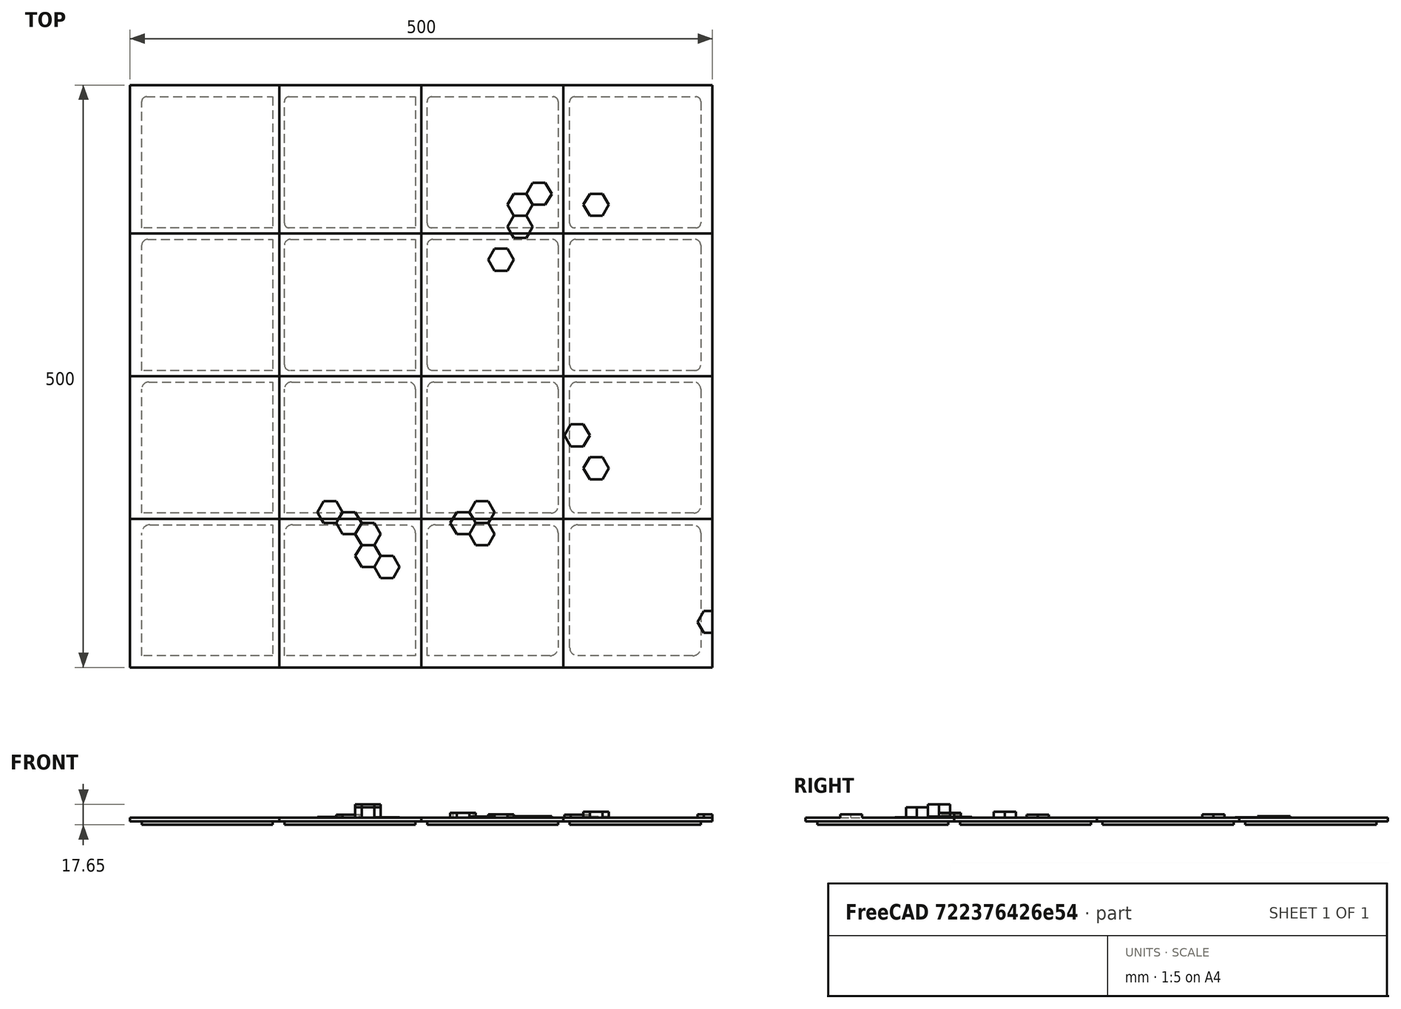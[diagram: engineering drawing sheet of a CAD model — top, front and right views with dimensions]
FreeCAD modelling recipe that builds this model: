
FCSTD DOCUMENT  (FreeCAD 0.17R13541 (Git))
Label: division_map_positive
License: All rights reserved
LicenseURL: http://en.wikipedia.org/wiki/All_rights_reserved
objects: Drawing::FeatureViewPart×48, Part::MultiCommon×16, Part::Mirroring×12, Part::Extrusion×4, Part::FeaturePython×2, Part::Cut×1, Drawing::FeaturePage×1
note: 35 computed .brp shape members not serialized (recipe doc carries the construction recipe); baked Part::Feature solids carry a one-line shape summary decoded from their .brp

FEATURE [Part::FeaturePython] Clone  label="Body001"  # WARN: FeaturePython — macro-defined, semantics opaque (R4)
  AttacherType = Attacher::AttachEngine3D
  Fuse = false
  Placement = pos=(0,0,3) rot=(0,0,1;0rad)
  Scale = (1,1,1)
FEATURE [Part::FeaturePython] Clone002  # WARN: FeaturePython — macro-defined, semantics opaque (R4)
  AttacherType = Attacher::AttachEngine3D
  Fuse = false
  Placement = pos=(0,0,0) rot=(0,0,1;1.5708rad)
  Scale = (1,1,1)
FEATURE [Part::Extrusion] Extrude  label="A1"
  Dir = (0,0,1)
  DirMode = 2
  FaceMakerClass = Part::FaceMakerBullseye
  LengthFwd = 50
  LengthRev = 0
  Solid = true
  Symmetric = true
FEATURE [Part::Extrusion] Extrude001  label="B1"
  Dir = (0,0,1)
  DirMode = 2
  FaceMakerClass = Part::FaceMakerBullseye
  LengthFwd = 50
  LengthRev = 0
  Solid = true
  Symmetric = true
FEATURE [Part::Extrusion] Extrude003  label="A2"
  Dir = (0,0,1)
  DirMode = 2
  FaceMakerClass = Part::FaceMakerBullseye
  LengthFwd = 50
  LengthRev = 0
  Solid = true
  Symmetric = true
FEATURE [Part::Extrusion] Extrude002  label="B2"
  Dir = (0,0,1)
  DirMode = 2
  FaceMakerClass = Part::FaceMakerBullseye
  LengthFwd = 70
  LengthRev = 0
  Solid = true
  Symmetric = true
FEATURE [Part::Mirroring] Part__Mirroring007  label="B3"
  Base = (0,0,0)
  Normal = (1,0,0)
  Source = -> Extrude002
FEATURE [Part::Mirroring] Part__Mirroring010  label="A3"
  Base = (0,0,0)
  Normal = (1,0,0)
  Source = -> Extrude003
FEATURE [Part::Mirroring] Part__Mirroring001  label="A4"
  Base = (0,0,0)
  Normal = (1,0,0)
  Source = -> Extrude
FEATURE [Part::Mirroring] Part__Mirroring004  label="B4"
  Base = (0,0,0)
  Normal = (1,0,0)
  Source = -> Extrude001
FEATURE [Part::Mirroring] Part__Mirroring006  label="C2"
  Base = (0,0,0)
  Normal = (0,1,0)
  Source = -> Extrude002
FEATURE [Part::Mirroring] Part__Mirroring008  label="C3"
  Base = (0,0,0)
  Normal = (1,0,0)
  Source = -> Part__Mirroring006
FEATURE [Part::Mirroring] Part__Mirroring003  label="C1"
  Base = (0,0,0)
  Normal = (0,1,0)
  Source = -> Extrude001
FEATURE [Part::Mirroring] Part__Mirroring005  label="C4"
  Base = (0,0,0)
  Normal = (1,0,0)
  Source = -> Part__Mirroring003
FEATURE [Part::Mirroring] Part__Mirroring  label="D1"
  Base = (0,0,0)
  Normal = (0,1,0)
  Source = -> Extrude
FEATURE [Part::Mirroring] Part__Mirroring009  label="D2"
  Base = (0,0,0)
  Normal = (0,1,0)
  Source = -> Extrude003
FEATURE [Part::Mirroring] Part__Mirroring011  label="D3"
  Base = (0,0,0)
  Normal = (1,0,0)
  Source = -> Part__Mirroring009
FEATURE [Part::Mirroring] Part__Mirroring002  label="D4"
  Base = (0,0,0)
  Normal = (1,0,0)
  Source = -> Part__Mirroring
FEATURE [Part::Cut] Cut  label="data_map"
  Base = -> Clone002
  Tool = -> Clone
FEATURE [Part::MultiCommon] Common  label="A1_cut"
  Shapes = -> [Extrude,Cut]
FEATURE [Part::MultiCommon] Common001  label="A2_cut"
  Shapes = -> [Cut,Extrude003]
FEATURE [Part::MultiCommon] Common002  label="A3_cut"
  Shapes = -> [Cut,Part__Mirroring010]
FEATURE [Part::MultiCommon] Common003  label="A4_cut"
  Shapes = -> [Cut,Part__Mirroring001]
FEATURE [Part::MultiCommon] Common004  label="B1_cut"
  Shapes = -> [Cut,Extrude001]
FEATURE [Part::MultiCommon] Common005  label="B2_cut"
  Shapes = -> [Extrude002,Cut]
FEATURE [Part::MultiCommon] Common006  label="B3_cut"
  Shapes = -> [Cut,Part__Mirroring007]
FEATURE [Part::MultiCommon] Common007  label="B4_cut"
  Shapes = -> [Cut,Part__Mirroring004]
FEATURE [Part::MultiCommon] Common008  label="C1_cut"
  Shapes = -> [Cut,Part__Mirroring003]
FEATURE [Part::MultiCommon] Common009  label="C2_cut"
  Shapes = -> [Cut,Part__Mirroring006]
FEATURE [Part::MultiCommon] Common010  label="C3_cut"
  Shapes = -> [Cut,Part__Mirroring008]
FEATURE [Part::MultiCommon] Common011  label="C4_cut"
  Shapes = -> [Cut,Part__Mirroring005]
FEATURE [Part::MultiCommon] Common012  label="D1_cut"
  Shapes = -> [Cut,Part__Mirroring]
FEATURE [Part::MultiCommon] Common013  label="D2_cut"
  Shapes = -> [Part__Mirroring009,Cut]
FEATURE [Part::MultiCommon] Common014  label="D3_cut"
  Shapes = -> [Part__Mirroring011,Cut]
FEATURE [Part::MultiCommon] Common015  label="D4_cut"
  Shapes = -> [Cut,Part__Mirroring002]
FEATURE [Drawing::FeatureViewPart] Ortho  label="Ortho_0_0"
  Direction = (1,0,0)
  HiddenWidth = 0.15
  LineWidth = 0.35
  Rotation = -90
  ShowHiddenLines = false
  ShowSmoothLines = false
  Source = -> Common
  Tolerance = 0.05
  ViewResult = <g id="Ortho_0_0"\n   transform="rotate(-90,134.29,687.126) translate(134.29,687.126) scale(1,1)"\n  >\n<g   fill="none"\n   stroke="rgb(0, 0, 0)"\n   stroke-linecap="butt"\n   stroke-linejoin="miter"\n   stroke-width="0.350000"\n   transform="scale(1,-1)"\n  >\n<path id= "1" d=" M 3 -250 L 6 -250 " />\n<path id= "2" d=" M 3 -250 L 3 -122.5 " />\n<path id= "3" d=" M 6 -122.5 L 6 -250 " />\n<path id= "4" d=" M 3 -122.5 L 6 -122.5 " />\n<path id= "5" d=" M 3 -240 L 0 -240 " />\n<path id= "6" d=" M 3 -127.5 L 0 -127.5 " />\n<path id= "7" d=" M 0 -127.5 L 0 -240 " />\n</g>\n</g>
  Visible = false
  X = 134.29
  Y = 687.126
FEATURE [Drawing::FeatureViewPart] Ortho001  label="Ortho_0_1"
  Direction = (0,0,1)
  HiddenWidth = 0.15
  LineWidth = 0.35
  Rotation = 90
  ShowHiddenLines = false
  ShowSmoothLines = false
  Source = -> Common
  Tolerance = 0.05
  ViewResult = <g id="Ortho_0_1"\n   transform="rotate(90,134.29,527.016) translate(134.29,527.016) scale(1,1)"\n  >\n<g   fill="none"\n   stroke="rgb(0, 0, 0)"\n   stroke-linecap="butt"\n   stroke-linejoin="miter"\n   stroke-width="0.350000"\n   transform="scale(1,-1)"\n  >\n<path id= "1" d=" M -250 250 L -121.905 250 " />\n<path id= "2" d=" M -121.905 122.5 L -121.905 250 " />\n<path id= "3" d=" M -250 122.5 L -250 250 " />\n<path id= "4" d=" M -250 122.5 L -121.905 122.5 " />\n</g>\n</g>
  Visible = false
  X = 134.29
  Y = 527.016
FEATURE [Drawing::FeatureViewPart] Ortho002  label="Ortho_1_1"
  Direction = (0.57735,0.57735,0.57735)
  HiddenWidth = 0.15
  LineWidth = 0.35
  Rotation = 120
  ShowHiddenLines = false
  ShowSmoothLines = false
  Source = -> Common
  Tolerance = 0.05
  ViewResult = <g id="Ortho_1_1"\n   transform="rotate(120,614.083,343.391) translate(614.083,343.391) scale(1,1)"\n  >\n<g   fill="none"\n   stroke="rgb(0, 0, 0)"\n   stroke-linecap="butt"\n   stroke-linejoin="miter"\n   stroke-width="0.350000"\n   transform="scale(1,-1)"\n  >\n<path id= "1" d=" M -88.3213 252.667 L -178.898 304.961 " />\n<path id= "2" d=" M -88.3213 252.667 L -90.4426 251.442 " />\n<path id= "3" d=" M -181.019 303.737 L -90.4426 251.442 " />\n<path id= "4" d=" M -178.898 304.961 L -181.019 303.737 " />\n<path id= "5" d=" M -88.3213 252.667 L -88.3213 148.564 " />\n<path id= "6" d=" M -90.4426 147.339 L -90.4426 251.442 " />\n<path id= "7" d=" M -88.3213 148.564 L -90.4426 147.339 " />\n<path id= "8" d=" M -181.019 199.633 L -181.019 303.737 " />\n<path id= "9" d=" M -181.019 199.633 L -90.4426 147.339 " />\n</g>\n</g>
  Visible = false
  X = 614.083
  Y = 343.391
FEATURE [Drawing::FeatureViewPart] Ortho003  label="Ortho_0_002"
  Direction = (1,0,0)
  HiddenWidth = 0.15
  LineWidth = 0.35
  Rotation = -90
  ShowHiddenLines = false
  ShowSmoothLines = false
  Source = -> Common001
  Tolerance = 0.05
  ViewResult = <g id="Ortho_0_002"\n   transform="rotate(-90,142.543,678.874) translate(142.543,678.874) scale(1,1)"\n  >\n<g   fill="none"\n   stroke="rgb(0, 0, 0)"\n   stroke-linecap="butt"\n   stroke-linejoin="miter"\n   stroke-width="0.350000"\n   transform="scale(1,-1)"\n  >\n<path id= "1" d=" M 6 -250 L 6 -122.5 " />\n<path id= "2" d=" M 3 -250 L 6 -250 " />\n<path id= "3" d=" M 3 -122.5 L 3 -250 " />\n<path id= "4" d=" M 3 -122.5 L 6 -122.5 " />\n<path id= "5" d=" M 3 -240 L 0 -240 " />\n<path id= "6" d=" M 3 -127.5 L 0 -127.5 " />\n<path id= "7" d=" M 0 -127.5 L 0 -240 " />\n</g>\n</g>
  Visible = false
  X = 142.543
  Y = 678.874
FEATURE [Drawing::FeatureViewPart] Ortho004  label="Ortho_0_003"
  Direction = (0,0,1)
  HiddenWidth = 0.15
  LineWidth = 0.35
  Rotation = 90
  ShowHiddenLines = false
  ShowSmoothLines = false
  Source = -> Common001
  Tolerance = 0.05
  ViewResult = <g id="Ortho_0_003"\n   transform="rotate(90,142.543,397.889) translate(142.543,397.889) scale(1,1)"\n  >\n<g   fill="none"\n   stroke="rgb(0, 0, 0)"\n   stroke-linecap="butt"\n   stroke-linejoin="miter"\n   stroke-width="0.350000"\n   transform="scale(1,-1)"\n  >\n<path id= "1" d=" M -121.905 250 L -5.68434e-14 250 " />\n<path id= "2" d=" M 0 250 L 0 122.5 " />\n<path id= "3" d=" M 0 122.5 L -121.905 122.5 " />\n<path id= "4" d=" M -121.905 250 L -121.905 122.5 " />\n</g>\n</g>
  Visible = false
  X = 142.543
  Y = 397.889
FEATURE [Drawing::FeatureViewPart] Ortho005  label="Ortho_1_002"
  Direction = (0.57735,0.57735,0.57735)
  HiddenWidth = 0.15
  LineWidth = 0.35
  Rotation = 120
  ShowHiddenLines = false
  ShowSmoothLines = false
  Source = -> Common001
  Tolerance = 0.05
  ViewResult = <g id="Ortho_1_002"\n   transform="rotate(120,706.598,288.234) translate(706.598,288.234) scale(1,1)"\n  >\n<g   fill="none"\n   stroke="rgb(0, 0, 0)"\n   stroke-linecap="butt"\n   stroke-linejoin="miter"\n   stroke-width="0.350000"\n   transform="scale(1,-1)"\n  >\n<path id= "1" d=" M -90.4426 251.442 L -4.24264 201.675 " />\n<path id= "2" d=" M -4.24264 201.675 L -4.24264 97.5713 " />\n<path id= "3" d=" M -4.24264 97.5713 L -90.4426 147.339 " />\n<path id= "4" d=" M -90.4426 251.442 L -90.4426 147.339 " />\n<path id= "5" d=" M -2.12132 202.899 L -4.24264 201.675 " />\n<path id= "6" d=" M -88.3213 252.667 L -90.4426 251.442 " />\n<path id= "7" d=" M -2.12132 202.899 L -88.3213 252.667 " />\n<path id= "8" d=" M -2.12132 98.7961 L -2.12132 202.899 " />\n<path id= "9" d=" M -2.12132 98.7961 L -4.24264 97.5713 " />\n</g>\n</g>
  Visible = false
  X = 706.598
  Y = 288.234
FEATURE [Drawing::FeatureViewPart] Ortho006  label="Ortho_0_004"
  Direction = (1,0,0)
  HiddenWidth = 0.15
  LineWidth = 0.35
  Rotation = -90
  ShowHiddenLines = false
  ShowSmoothLines = false
  Source = -> Common002
  Tolerance = 0.05
  ViewResult = <g id="Ortho_0_004"\n   transform="rotate(-90,413.25,1262.38) translate(413.25,1262.38) scale(1,1)"\n  >\n<g   fill="none"\n   stroke="rgb(0, 0, 0)"\n   stroke-linecap="butt"\n   stroke-linejoin="miter"\n   stroke-width="0.350000"\n   transform="scale(1,-1)"\n  >\n<path id= "1" d=" M 6 -250 L 6 -122.5 " />\n<path id= "2" d=" M 3 -250 L 6 -250 " />\n<path id= "3" d=" M 3 -122.5 L 3 -250 " />\n<path id= "4" d=" M 3 -122.5 L 6 -122.5 " />\n<path id= "5" d=" M 6.47083 -122.5 L 6 -122.5 " />\n<path id= "6" d=" M 6.47083 -122.5 L 6.47083 -128.407 " />\n<path id= "7" d=" M 6 -128.407 L 6.47083 -128.407 " />\n<path id= "8" d=" M 6.47083 -128.407 L 6.47083 -137.831 " />\n<path id= "9" d=" M 6 -137.831 L 6.47083 -137.831 " />\n<path id= "10" d=" M 6 -137.833 L 7.51587 -137.833 " />\n<path id= "11" d=" M 7.51587 -137.833 L 7.51587 -147.257 " />\n<path id= "12" d=" M 6 -147.257 L 7.51587 -147.257 " />\n<path id= "13" d=" M 7.51587 -147.257 L 7.51587 -156.682 " />\n<path id= "14" d=" M 7.49444 -156.682 L 7.51587 -156.682 " />\n<path id= "15" d=" M 6 -147.258 L 7.49444 -147.258 " />\n<path id= "16" d=" M 7.49444 -147.258 L 7.49444 -156.682 " />\n<path id= "17" d=" M 6 -156.682 L 7.49444 -156.682 " />\n<path id= "18" d=" M 7.49444 -156.682 L 7.49444 -166.107 " />\n<path id= "19" d=" M 6 -166.107 L 7.49444 -166.107 " />\n<path id= "20" d=" M 3 -240 L 0 -240 " />\n<path d="M0,-240 Q0,-239.987 0,-239.975  Q0,-239.937 0,-239.9  Q0,-239.838 0,-239.776  Q0,-239.69 0,-239.604  Q0,-239.495 0,-239.387  Q0,-239.257 0,-239.127  Q0,-238.978 0,-238.828  Q0,-238.661 0,-238.494  Q0,-238.311 0,-238.128  Q0,-237.932 0,-237.736  Q0,-237.528 0,-237.321  Q0,-237.106 0,-236.89  Q0,-236.449 0,-236 " /><path id= "22" d=" M 3 -127.5 L 0 -127.5 " />\n<path id= "23" d=" M 0 -127.5 L 0 -236 " />\n</g>\n</g>
  Visible = false
  X = 413.25
  Y = 1262.38
FEATURE [Drawing::FeatureViewPart] Ortho007  label="Ortho_0_005"
  Direction = (0,0,1)
  HiddenWidth = 0.15
  LineWidth = 0.35
  Rotation = 90
  ShowHiddenLines = false
  ShowSmoothLines = false
  Source = -> Common002
  Tolerance = 0.05
  ViewResult = <g id="Ortho_0_005"\n   transform="rotate(90,413.25,329.547) translate(413.25,329.547) scale(1,1)"\n  >\n<g   fill="none"\n   stroke="rgb(0, 0, 0)"\n   stroke-linecap="butt"\n   stroke-linejoin="miter"\n   stroke-width="0.350000"\n   transform="scale(1,-1)"\n  >\n<path id= "1" d=" M -5.68434e-14 250 L 121.905 250 " />\n<path id= "2" d=" M 121.905 250 L 121.905 122.5 " />\n<path id= "3" d=" M 92.2812 122.5 L 121.905 122.5 " />\n<path id= "4" d=" M 0 122.5 L 77.3374 122.5 " />\n<path id= "5" d=" M 0 250 L 0 122.5 " />\n<path id= "6" d=" M 77.3374 122.5 L 92.2812 122.5 " />\n<path id= "7" d=" M 92.2812 122.5 L 95.6916 128.407 " />\n<path id= "8" d=" M 95.6916 128.407 L 90.2504 137.831 " />\n<path id= "9" d=" M 90.2504 137.831 L 79.3681 137.831 " />\n<path id= "10" d=" M 79.3681 137.831 L 73.927 128.407 " />\n<path id= "11" d=" M 73.927 128.407 L 77.3374 122.5 " />\n<path id= "12" d=" M 79.3681 137.833 L 90.2504 137.833 " />\n<path id= "13" d=" M 90.2504 137.833 L 95.6916 147.257 " />\n<path id= "14" d=" M 73.927 147.257 L 79.3681 137.833 " />\n<path id= "15" d=" M 95.6916 147.257 L 90.2504 156.682 " />\n<path id= "16" d=" M 79.3681 156.682 L 73.927 147.257 " />\n<path id= "17" d=" M 90.2504 156.682 L 79.3681 156.682 " />\n<path id= "18" d=" M 95.6929 147.258 L 106.575 147.258 " />\n<path id= "19" d=" M 106.575 147.258 L 112.016 156.682 " />\n<path id= "20" d=" M 90.2518 156.682 L 95.6929 147.258 " />\n<path id= "21" d=" M 112.016 156.682 L 106.575 166.107 " />\n<path id= "22" d=" M 95.6929 166.107 L 90.2518 156.682 " />\n<path id= "23" d=" M 106.575 166.107 L 95.6929 166.107 " />\n</g>\n</g>
  Visible = false
  X = 413.25
  Y = 329.547
FEATURE [Drawing::FeatureViewPart] Ortho008  label="Ortho_1_003"
  Direction = (0.57735,0.57735,0.57735)
  HiddenWidth = 0.15
  LineWidth = 0.35
  Rotation = 120
  ShowHiddenLines = false
  ShowSmoothLines = false
  Source = -> Common002
  Tolerance = 0.05
  ViewResult = <blob: 3069 chars omitted>
  Visible = false
  X = 1578.02
  Y = 292.648
FEATURE [Drawing::FeatureViewPart] Ortho009  label="Ortho_0_006"
  Direction = (1,0,0)
  HiddenWidth = 0.15
  LineWidth = 0.35
  Rotation = -90
  ShowHiddenLines = false
  ShowSmoothLines = false
  Source = -> Common003
  Tolerance = 0.05
  ViewResult = <g id="Ortho_0_006"\n   transform="rotate(-90,413.25,1287.07) translate(413.25,1287.07) scale(1,1)"\n  >\n<g   fill="none"\n   stroke="rgb(0, 0, 0)"\n   stroke-linecap="butt"\n   stroke-linejoin="miter"\n   stroke-width="0.350000"\n   transform="scale(1,-1)"\n  >\n<path id= "1" d=" M 6 -250 L 6 -122.5 " />\n<path id= "2" d=" M 3 -250 L 6 -250 " />\n<path id= "3" d=" M 3 -122.5 L 6 -122.5 " />\n<path id= "4" d=" M 3 -122.5 L 3 -250 " />\n<path id= "5" d=" M 6 -137.833 L 7.37324 -137.833 " />\n<path id= "6" d=" M 7.37324 -137.833 L 7.37324 -147.257 " />\n<path id= "7" d=" M 6 -147.257 L 7.37324 -147.257 " />\n<path id= "8" d=" M 7.37324 -147.257 L 7.37324 -156.682 " />\n<path id= "9" d=" M 6 -156.682 L 7.37324 -156.682 " />\n<path id= "10" d=" M 3 -240 L 0 -240 " />\n<path d="M0,-240 Q0,-239.987 0,-239.975  Q0,-239.937 0,-239.9  Q0,-239.838 0,-239.776  Q0,-239.69 0,-239.604  Q0,-239.495 0,-239.387  Q0,-239.257 0,-239.127  Q0,-238.978 0,-238.828  Q0,-238.661 0,-238.494  Q0,-238.311 0,-238.128  Q0,-237.932 0,-237.736  Q0,-237.528 0,-237.321  Q0,-237.106 0,-236.89  Q0,-236.449 0,-236 " /><path id= "12" d=" M 0 -131.5 L 0 -236 " />\n<path id= "13" d=" M 3 -127.5 L 0 -127.5 " />\n<path d="M0,-131.5 L0,-131.052  L0,-130.61  L0,-130.179  L0,-129.764  L0,-129.372  L0,-129.006  L0,-128.672  L0,-128.373  L0,-128.113  L0,-127.896  L0,-127.724  L0,-127.6  L0,-127.525  L0,-127.5 " /></g>\n</g>
  Visible = false
  X = 413.25
  Y = 1287.07
FEATURE [Drawing::FeatureViewPart] Ortho010  label="Ortho_0_007"
  Direction = (0,0,1)
  HiddenWidth = 0.15
  LineWidth = 0.35
  Rotation = 90
  ShowHiddenLines = false
  ShowSmoothLines = false
  Source = -> Common003
  Tolerance = 0.05
  ViewResult = <g id="Ortho_0_007"\n   transform="rotate(90,413.25,204.547) translate(413.25,204.547) scale(1,1)"\n  >\n<g   fill="none"\n   stroke="rgb(0, 0, 0)"\n   stroke-linecap="butt"\n   stroke-linejoin="miter"\n   stroke-width="0.350000"\n   transform="scale(1,-1)"\n  >\n<path id= "1" d=" M 121.905 250 L 250 250 " />\n<path id= "2" d=" M 250 250 L 250 122.5 " />\n<path id= "3" d=" M 121.905 122.5 L 250 122.5 " />\n<path id= "4" d=" M 121.905 250 L 121.905 122.5 " />\n<path id= "5" d=" M 144.667 137.833 L 155.549 137.833 " />\n<path id= "6" d=" M 155.549 137.833 L 160.991 147.257 " />\n<path id= "7" d=" M 139.226 147.257 L 144.667 137.833 " />\n<path id= "8" d=" M 160.991 147.257 L 155.549 156.682 " />\n<path id= "9" d=" M 144.667 156.682 L 139.226 147.257 " />\n<path id= "10" d=" M 155.549 156.682 L 144.667 156.682 " />\n</g>\n</g>
  Visible = false
  X = 413.25
  Y = 204.547
FEATURE [Drawing::FeatureViewPart] Ortho011  label="Ortho_1_004"
  Direction = (0.57735,0.57735,0.57735)
  HiddenWidth = 0.15
  LineWidth = 0.35
  Rotation = 120
  ShowHiddenLines = false
  ShowSmoothLines = false
  Source = -> Common003
  Tolerance = 0.05
  ViewResult = <g id="Ortho_1_004"\n   transform="rotate(120,1691.17,241.559) translate(1691.17,241.559) scale(1,1)"\n  >\n<g   fill="none"\n   stroke="rgb(0, 0, 0)"\n   stroke-linecap="butt"\n   stroke-linejoin="miter"\n   stroke-width="0.350000"\n   transform="scale(1,-1)"\n  >\n<path id= "1" d=" M 81.9574 151.907 L 172.534 99.6126 " />\n<path id= "2" d=" M 172.534 99.6126 L 172.534 -4.49073 " />\n<path id= "3" d=" M 81.9574 47.8038 L 172.534 -4.49073 " />\n<path id= "4" d=" M 81.9574 151.907 L 81.9574 47.8038 " />\n<path id= "5" d=" M 109.595 52.0614 L 105.747 46.5878 " />\n<path id= "6" d=" M 105.747 61.9777 L 109.595 52.0614 " />\n<path id= "7" d=" M 98.0524 66.4204 L 105.747 61.9777 " />\n<path id= "8" d=" M 174.655 100.837 L 172.534 99.6126 " />\n<path id= "9" d=" M 84.0787 153.132 L 81.9574 151.907 " />\n<path id= "10" d=" M 174.655 100.837 L 84.0787 153.132 " />\n<path id= "11" d=" M 174.655 -3.26599 L 172.534 -4.49073 " />\n<path id= "12" d=" M 174.655 -3.26599 L 174.655 100.837 " />\n<path id= "13" d=" M 97.0814 50.4698 L 104.776 46.0272 " />\n<path id= "14" d=" M 105.747 46.5878 L 104.776 46.0272 " />\n<path id= "15" d=" M 104.776 46.0272 L 108.624 51.5008 " />\n<path id= "16" d=" M 109.595 52.0614 L 108.624 51.5008 " />\n<path id= "17" d=" M 93.2339 60.3861 L 97.0814 50.4698 " />\n<path id= "18" d=" M 108.624 51.5008 L 104.776 61.417 " />\n<path id= "19" d=" M 105.747 61.9777 L 104.776 61.417 " />\n<path id= "20" d=" M 98.0524 66.4204 L 97.0814 65.8597 " />\n<path id= "21" d=" M 97.0814 65.8597 L 93.2339 60.3861 " />\n<path id= "22" d=" M 104.776 61.417 L 97.0814 65.8597 " />\n</g>\n</g>
  Visible = false
  X = 1691.17
  Y = 241.559
FEATURE [Drawing::FeatureViewPart] Ortho012  label="Ortho_0_008"
  Direction = (1,0,0)
  HiddenWidth = 0.15
  LineWidth = 0.35
  Rotation = -90
  ShowHiddenLines = false
  ShowSmoothLines = false
  Source = -> Common004
  Tolerance = 0.05
  ViewResult = <g id="Ortho_0_008"\n   transform="rotate(-90,538.25,1286.38) translate(538.25,1286.38) scale(1,1)"\n  >\n<g   fill="none"\n   stroke="rgb(0, 0, 0)"\n   stroke-linecap="butt"\n   stroke-linejoin="miter"\n   stroke-width="0.350000"\n   transform="scale(1,-1)"\n  >\n<path id= "1" d=" M 6 0 L 6 -122.5 " />\n<path id= "2" d=" M 3 -122.5 L 6 -122.5 " />\n<path id= "3" d=" M 3 -122.5 L 3 0 " />\n<path id= "4" d=" M 3 0 L 6 0 " />\n<path id= "5" d=" M 3 -117.5 L 0 -117.5 " />\n<path id= "6" d=" M 3 -5 L 0 -5 " />\n<path id= "7" d=" M 0 -5 L 0 -117.5 " />\n</g>\n</g>
  Visible = false
  X = 538.25
  Y = 1286.38
FEATURE [Drawing::FeatureViewPart] Ortho013  label="Ortho_0_009"
  Direction = (0,0,1)
  HiddenWidth = 0.15
  LineWidth = 0.35
  Rotation = 90
  ShowHiddenLines = false
  ShowSmoothLines = false
  Source = -> Common004
  Tolerance = 0.05
  ViewResult = <g id="Ortho_0_009"\n   transform="rotate(90,538.25,576.453) translate(538.25,576.453) scale(1,1)"\n  >\n<g   fill="none"\n   stroke="rgb(0, 0, 0)"\n   stroke-linecap="butt"\n   stroke-linejoin="miter"\n   stroke-width="0.350000"\n   transform="scale(1,-1)"\n  >\n<path id= "1" d=" M -250 -5.68434e-14 L -250 122.5 " />\n<path id= "2" d=" M -121.905 122.5 L -250 122.5 " />\n<path id= "3" d=" M -121.905 0 L -121.905 122.5 " />\n<path id= "4" d=" M -250 0 L -121.905 0 " />\n</g>\n</g>
  Visible = false
  X = 538.25
  Y = 576.453
FEATURE [Drawing::FeatureViewPart] Ortho014  label="Ortho_1_005"
  Direction = (0.57735,0.57735,0.57735)
  HiddenWidth = 0.15
  LineWidth = 0.35
  Rotation = 120
  ShowHiddenLines = false
  ShowSmoothLines = false
  Source = -> Common004
  Tolerance = 0.05
  ViewResult = <g id="Ortho_1_005"\n   transform="rotate(120,1516.58,443.859) translate(1516.58,443.859) scale(1,1)"\n  >\n<g   fill="none"\n   stroke="rgb(0, 0, 0)"\n   stroke-linecap="butt"\n   stroke-linejoin="miter"\n   stroke-width="0.350000"\n   transform="scale(1,-1)"\n  >\n<path id= "1" d=" M -181.019 99.6126 L -181.019 199.633 " />\n<path id= "2" d=" M -90.4426 147.339 L -181.019 199.633 " />\n<path id= "3" d=" M -90.4426 47.3181 L -90.4426 147.339 " />\n<path id= "4" d=" M -181.019 99.6126 L -90.4426 47.3181 " />\n<path id= "5" d=" M -178.898 200.858 L -181.019 199.633 " />\n<path id= "6" d=" M -178.898 200.858 L -88.3213 148.564 " />\n<path id= "7" d=" M -88.3213 148.564 L -90.4426 147.339 " />\n<path id= "8" d=" M -88.3213 148.564 L -88.3213 48.5428 " />\n<path id= "9" d=" M -88.3213 48.5428 L -90.4426 47.3181 " />\n</g>\n</g>
  Visible = false
  X = 1516.58
  Y = 443.859
FEATURE [Drawing::FeatureViewPart] Ortho015  label="Ortho_0_010"
  Direction = (1,0,0)
  HiddenWidth = 0.15
  LineWidth = 0.35
  Rotation = -90
  ShowHiddenLines = false
  ShowSmoothLines = false
  Source = -> Common005
  Tolerance = 0.05
  ViewResult = <g id="Ortho_0_010"\n   transform="rotate(-90,538.25,1261.62) translate(538.25,1261.62) scale(1,1)"\n  >\n<g   fill="none"\n   stroke="rgb(0, 0, 0)"\n   stroke-linecap="butt"\n   stroke-linejoin="miter"\n   stroke-width="0.350000"\n   transform="scale(1,-1)"\n  >\n<path id= "1" d=" M 3 -122.5 L 3 0 " />\n<path id= "2" d=" M 3 0 L 6 0 " />\n<path id= "3" d=" M 6 0 L 6 -122.5 " />\n<path id= "4" d=" M 3 -122.5 L 6 -122.5 " />\n<path id= "5" d=" M 3 -117.5 L 0 -117.5 " />\n<path id= "6" d=" M 3 -5 L 0 -5 " />\n<path id= "7" d=" M 0 -5 L 0 -117.5 " />\n</g>\n</g>
  Visible = false
  X = 538.25
  Y = 1261.62
FEATURE [Drawing::FeatureViewPart] Ortho016  label="Ortho_0_011"
  Direction = (0,0,1)
  HiddenWidth = 0.15
  LineWidth = 0.35
  Rotation = 90
  ShowHiddenLines = false
  ShowSmoothLines = false
  Source = -> Common005
  Tolerance = 0.05
  ViewResult = <g id="Ortho_0_011"\n   transform="rotate(90,538.25,451.453) translate(538.25,451.453) scale(1,1)"\n  >\n<g   fill="none"\n   stroke="rgb(0, 0, 0)"\n   stroke-linecap="butt"\n   stroke-linejoin="miter"\n   stroke-width="0.350000"\n   transform="scale(1,-1)"\n  >\n<path id= "1" d=" M -121.905 122.5 L -121.905 0 " />\n<path id= "2" d=" M -121.905 0 L 0 0 " />\n<path id= "3" d=" M -121.905 122.5 L 0 122.5 " />\n<path id= "4" d=" M 0 0 L 0 122.5 " />\n</g>\n</g>
  Visible = false
  X = 538.25
  Y = 451.453
FEATURE [Drawing::FeatureViewPart] Ortho017  label="Ortho_1_006"
  Direction = (0.57735,0.57735,0.57735)
  HiddenWidth = 0.15
  LineWidth = 0.35
  Rotation = 120
  ShowHiddenLines = false
  ShowSmoothLines = false
  Source = -> Common005
  Tolerance = 0.05
  ViewResult = <g id="Ortho_1_006"\n   transform="rotate(120,1580.21,392.828) translate(1580.21,392.828) scale(1,1)"\n  >\n<g   fill="none"\n   stroke="rgb(0, 0, 0)"\n   stroke-linecap="butt"\n   stroke-linejoin="miter"\n   stroke-width="0.350000"\n   transform="scale(1,-1)"\n  >\n<path id= "1" d=" M -90.4426 147.339 L -90.4426 47.3181 " />\n<path id= "2" d=" M -88.3213 148.564 L -90.4426 147.339 " />\n<path id= "3" d=" M -2.12132 98.7961 L -2.12132 -1.22474 " />\n<path id= "4" d=" M -2.12132 98.7961 L -88.3213 148.564 " />\n<path id= "5" d=" M -2.12132 -1.22474 L -4.24264 -2.44949 " />\n<path id= "6" d=" M -90.4426 47.3181 L -4.24264 -2.44949 " />\n<path id= "7" d=" M -90.4426 147.339 L -4.24264 97.5713 " />\n<path id= "8" d=" M -4.24264 -2.44949 L -4.24264 97.5713 " />\n<path id= "9" d=" M -2.12132 98.7961 L -4.24264 97.5713 " />\n</g>\n</g>
  Visible = false
  X = 1580.21
  Y = 392.828
FEATURE [Drawing::FeatureViewPart] Ortho018  label="Ortho_0_012"
  Direction = (1,0,0)
  HiddenWidth = 0.15
  LineWidth = 0.35
  Rotation = -90
  ShowHiddenLines = false
  ShowSmoothLines = false
  Source = -> Common006
  Tolerance = 0.05
  ViewResult = <g id="Ortho_0_012"\n   transform="rotate(-90,538.25,1263.1) translate(538.25,1263.1) scale(1,1)"\n  >\n<g   fill="none"\n   stroke="rgb(0, 0, 0)"\n   stroke-linecap="butt"\n   stroke-linejoin="miter"\n   stroke-width="0.350000"\n   transform="scale(1,-1)"\n  >\n<path id= "1" d=" M 6 0 L 6 -122.5 " />\n<path id= "2" d=" M 6.47083 -118.983 L 6.47083 -122.5 " />\n<path id= "3" d=" M 6.47083 -122.5 L 6 -122.5 " />\n<path id= "4" d=" M 6 -118.983 L 6.47083 -118.983 " />\n<path id= "5" d=" M 3 -122.5 L 6 -122.5 " />\n<path id= "6" d=" M 3 -122.5 L 3 0 " />\n<path id= "7" d=" M 3 0 L 6 0 " />\n<path id= "8" d=" M 6 -90.7074 L 8.9662 -90.7074 " />\n<path id= "9" d=" M 8.9662 -90.7074 L 8.9662 -100.132 " />\n<path id= "10" d=" M 6 -100.132 L 8.9662 -100.132 " />\n<path id= "11" d=" M 8.9662 -100.132 L 8.9662 -109.556 " />\n<path id= "12" d=" M 6 -109.556 L 8.9662 -109.556 " />\n<path id= "13" d=" M 3 -117.5 L 0 -117.5 " />\n<path d="M0,-117.5 Q0,-117.484 0,-117.469  Q0,-117.422 0,-117.375  Q0,-117.297 0,-117.219  Q0,-117.112 0,-117.005  Q0,-116.869 0,-116.734  Q0,-116.571 0,-116.409  Q0,-116.222 0,-116.036  Q0,-115.826 0,-115.617  Q0,-115.389 0,-115.16  Q0,-114.915 0,-114.669  Q0,-114.41 0,-114.151  Q0,-113.882 0,-113.613  Q0,-113.062 0,-112.5 " /><path id= "15" d=" M 3 -5 L 0 -5 " />\n<path id= "16" d=" M 0 -5 L 0 -112.5 " />\n</g>\n</g>
  Visible = false
  X = 538.25
  Y = 1263.1
FEATURE [Drawing::FeatureViewPart] Ortho019  label="Ortho_0_013"
  Direction = (0,0,1)
  HiddenWidth = 0.15
  LineWidth = 0.35
  Rotation = 90
  ShowHiddenLines = false
  ShowSmoothLines = false
  Source = -> Common006
  Tolerance = 0.05
  ViewResult = <g id="Ortho_0_013"\n   transform="rotate(90,538.25,329.547) translate(538.25,329.547) scale(1,1)"\n  >\n<g   fill="none"\n   stroke="rgb(0, 0, 0)"\n   stroke-linecap="butt"\n   stroke-linejoin="miter"\n   stroke-width="0.350000"\n   transform="scale(1,-1)"\n  >\n<path id= "1" d=" M 92.2812 122.5 L 121.905 122.5 " />\n<path id= "2" d=" M 121.905 0 L 121.905 122.5 " />\n<path id= "3" d=" M 0 0 L 121.905 0 " />\n<path id= "4" d=" M 0 122.5 L 0 0 " />\n<path id= "5" d=" M 0 122.5 L 77.3374 122.5 " />\n<path id= "6" d=" M 90.2504 118.983 L 92.2812 122.5 " />\n<path id= "7" d=" M 77.3374 122.5 L 92.2812 122.5 " />\n<path id= "8" d=" M 77.3374 122.5 L 79.3681 118.983 " />\n<path id= "9" d=" M 79.3681 118.983 L 90.2504 118.983 " />\n<path id= "10" d=" M 63.0434 90.7074 L 73.9257 90.7074 " />\n<path id= "11" d=" M 73.9257 90.7074 L 79.3668 100.132 " />\n<path id= "12" d=" M 57.6023 100.132 L 63.0434 90.7074 " />\n<path id= "13" d=" M 79.3668 100.132 L 73.9257 109.556 " />\n<path id= "14" d=" M 63.0434 109.556 L 57.6023 100.132 " />\n<path id= "15" d=" M 73.9257 109.556 L 63.0434 109.556 " />\n</g>\n</g>
  Visible = false
  X = 538.25
  Y = 329.547
FEATURE [Drawing::FeatureViewPart] Ortho020  label="Ortho_1_007"
  Direction = (0.57735,0.57735,0.57735)
  HiddenWidth = 0.15
  LineWidth = 0.35
  Rotation = 120
  ShowHiddenLines = false
  ShowSmoothLines = false
  Source = -> Common006
  Tolerance = 0.05
  ViewResult = <blob: 2126 chars omitted>
  Visible = false
  X = 1666.41
  Y = 344.271
FEATURE [Drawing::FeatureViewPart] Ortho021  label="Ortho_0_014"
  Direction = (1,0,0)
  HiddenWidth = 0.15
  LineWidth = 0.35
  Rotation = -90
  ShowHiddenLines = false
  ShowSmoothLines = false
  Source = -> Common007
  Tolerance = 0.05
  ViewResult = <g id="Ortho_0_014"\n   transform="rotate(-90,538.25,1286.38) translate(538.25,1286.38) scale(1,1)"\n  >\n<g   fill="none"\n   stroke="rgb(0, 0, 0)"\n   stroke-linecap="butt"\n   stroke-linejoin="miter"\n   stroke-width="0.350000"\n   transform="scale(1,-1)"\n  >\n<path id= "1" d=" M 6 -122.5 L 6 -5.68434e-14 " />\n<path id= "2" d=" M 3 0 L 6 0 " />\n<path id= "3" d=" M 3 -122.5 L 6 -122.5 " />\n<path id= "4" d=" M 3 0 L 3 -122.5 " />\n<path id= "5" d=" M 3 -117.5 L 0 -117.5 " />\n<path d="M0,-117.5 Q0,-117.484 0,-117.469  Q0,-117.422 0,-117.375  Q0,-117.297 0,-117.219  Q0,-117.112 0,-117.005  Q0,-116.869 0,-116.734  Q0,-116.571 0,-116.409  Q0,-116.222 0,-116.036  Q0,-115.826 0,-115.617  Q0,-115.389 0,-115.16  Q0,-114.915 0,-114.669  Q0,-114.41 0,-114.151  Q0,-113.882 0,-113.613  Q0,-113.062 0,-112.5 " /><path id= "7" d=" M 0 -10 L 0 -112.5 " />\n<path id= "8" d=" M 3 -5 L 0 -5 " />\n<path d="M0,-10 L0,-9.44018  L0,-8.8874  L0,-8.3486  L0,-7.83058  L0,-7.33984  L0,-6.88255  L0,-6.46447  L0,-6.09084  L0,-5.76638  L0,-5.49516  L0,-5.28058  L0,-5.12536  L0,-5.03144  L0,-5 " /></g>\n</g>
  Visible = false
  X = 538.25
  Y = 1286.38
FEATURE [Drawing::FeatureViewPart] Ortho022  label="Ortho_0_015"
  Direction = (0,0,1)
  HiddenWidth = 0.15
  LineWidth = 0.35
  Rotation = 90
  ShowHiddenLines = false
  ShowSmoothLines = false
  Source = -> Common007
  Tolerance = 0.05
  ViewResult = <g id="Ortho_0_015"\n   transform="rotate(90,538.25,204.547) translate(538.25,204.547) scale(1,1)"\n  >\n<g   fill="none"\n   stroke="rgb(0, 0, 0)"\n   stroke-linecap="butt"\n   stroke-linejoin="miter"\n   stroke-width="0.350000"\n   transform="scale(1,-1)"\n  >\n<path id= "1" d=" M 250 122.5 L 250 5.68434e-14 " />\n<path id= "2" d=" M 250 0 L 121.905 0 " />\n<path id= "3" d=" M 121.905 0 L 121.905 122.5 " />\n<path id= "4" d=" M 121.905 122.5 L 250 122.5 " />\n</g>\n</g>
  Visible = false
  X = 538.25
  Y = 204.547
FEATURE [Drawing::FeatureViewPart] Ortho023  label="Ortho_1_008"
  Direction = (0.57735,0.57735,0.57735)
  HiddenWidth = 0.15
  LineWidth = 0.35
  Rotation = 120
  ShowHiddenLines = false
  ShowSmoothLines = false
  Source = -> Common007
  Tolerance = 0.05
  ViewResult = <g id="Ortho_1_008"\n   transform="rotate(120,1779.56,292.029) translate(1779.56,292.029) scale(1,1)"\n  >\n<g   fill="none"\n   stroke="rgb(0, 0, 0)"\n   stroke-linecap="butt"\n   stroke-linejoin="miter"\n   stroke-width="0.350000"\n   transform="scale(1,-1)"\n  >\n<path id= "1" d=" M 172.534 -4.49073 L 172.534 -104.512 " />\n<path id= "2" d=" M 172.534 -104.512 L 81.9574 -52.2171 " />\n<path id= "3" d=" M 81.9574 -52.2171 L 81.9574 47.8038 " />\n<path id= "4" d=" M 81.9574 47.8038 L 172.534 -4.49073 " />\n<path id= "5" d=" M 174.655 -103.287 L 172.534 -104.512 " />\n<path id= "6" d=" M 174.655 -3.26599 L 172.534 -4.49073 " />\n<path id= "7" d=" M 174.655 -103.287 L 174.655 -3.26599 " />\n<path id= "8" d=" M 84.0787 49.0285 L 81.9574 47.8038 " />\n<path id= "9" d=" M 174.655 -3.26599 L 84.0787 49.0285 " />\n</g>\n</g>
  Visible = false
  X = 1779.56
  Y = 292.029
FEATURE [Drawing::FeatureViewPart] Ortho024  label="Ortho_0_016"
  Direction = (1,0,0)
  HiddenWidth = 0.15
  LineWidth = 0.35
  Rotation = -90
  ShowHiddenLines = false
  ShowSmoothLines = false
  Source = -> Common008
  Tolerance = 0.05
  ViewResult = <g id="Ortho_0_016"\n   transform="rotate(-90,660.75,1286.38) translate(660.75,1286.38) scale(1,1)"\n  >\n<g   fill="none"\n   stroke="rgb(0, 0, 0)"\n   stroke-linecap="butt"\n   stroke-linejoin="miter"\n   stroke-width="0.350000"\n   transform="scale(1,-1)"\n  >\n<path id= "1" d=" M 6 0 L 6 122.5 " />\n<path id= "2" d=" M 3 0 L 6 0 " />\n<path id= "3" d=" M 3 122.5 L 3 0 " />\n<path id= "4" d=" M 3 122.5 L 6 122.5 " />\n<path id= "5" d=" M 3 5 L 0 5 " />\n<path id= "6" d=" M 3 117.5 L 0 117.5 " />\n<path id= "7" d=" M 0 117.5 L 0 5 " />\n</g>\n</g>
  Visible = false
  X = 660.75
  Y = 1286.38
FEATURE [Drawing::FeatureViewPart] Ortho025  label="Ortho_0_017"
  Direction = (0,0,1)
  HiddenWidth = 0.15
  LineWidth = 0.35
  Rotation = 90
  ShowHiddenLines = false
  ShowSmoothLines = false
  Source = -> Common008
  Tolerance = 0.05
  ViewResult = <g id="Ortho_0_017"\n   transform="rotate(90,660.75,576.453) translate(660.75,576.453) scale(1,1)"\n  >\n<g   fill="none"\n   stroke="rgb(0, 0, 0)"\n   stroke-linecap="butt"\n   stroke-linejoin="miter"\n   stroke-width="0.350000"\n   transform="scale(1,-1)"\n  >\n<path id= "1" d=" M -250 -122.5 L -250 -5.68434e-14 " />\n<path id= "2" d=" M -250 0 L -121.905 0 " />\n<path id= "3" d=" M -121.905 0 L -121.905 -122.5 " />\n<path id= "4" d=" M -121.905 -122.5 L -250 -122.5 " />\n</g>\n</g>
  Visible = false
  X = 660.75
  Y = 576.453
FEATURE [Drawing::FeatureViewPart] Ortho026  label="Ortho_1_009"
  Direction = (0.57735,0.57735,0.57735)
  HiddenWidth = 0.15
  LineWidth = 0.35
  Rotation = 120
  ShowHiddenLines = false
  ShowSmoothLines = false
  Source = -> Common008
  Tolerance = 0.05
  ViewResult = <g id="Ortho_1_009"\n   transform="rotate(120,1603.2,493.87) translate(1603.2,493.87) scale(1,1)"\n  >\n<g   fill="none"\n   stroke="rgb(0, 0, 0)"\n   stroke-linecap="butt"\n   stroke-linejoin="miter"\n   stroke-width="0.350000"\n   transform="scale(1,-1)"\n  >\n<path id= "1" d=" M -181.019 -0.408248 L -181.019 99.6126 " />\n<path id= "2" d=" M -181.019 99.6126 L -90.4426 47.3181 " />\n<path id= "3" d=" M -90.4426 47.3181 L -90.4426 -52.7027 " />\n<path id= "4" d=" M -90.4426 -52.7027 L -181.019 -0.408248 " />\n<path id= "5" d=" M -178.898 100.837 L -181.019 99.6126 " />\n<path id= "6" d=" M -88.3213 48.5428 L -178.898 100.837 " />\n<path id= "7" d=" M -88.3213 48.5428 L -90.4426 47.3181 " />\n<path id= "8" d=" M -88.3213 -51.478 L -88.3213 48.5428 " />\n<path id= "9" d=" M -88.3213 -51.478 L -90.4426 -52.7027 " />\n</g>\n</g>
  Visible = false
  X = 1603.2
  Y = 493.87
FEATURE [Drawing::FeatureViewPart] Ortho027  label="Ortho_0_018"
  Direction = (1,0,0)
  HiddenWidth = 0.15
  LineWidth = 0.35
  Rotation = -90
  ShowHiddenLines = false
  ShowSmoothLines = false
  Source = -> Common009
  Tolerance = 0.05
  ViewResult = <g id="Ortho_0_018"\n   transform="rotate(-90,660.75,1263.02) translate(660.75,1263.02) scale(1,1)"\n  >\n<g   fill="none"\n   stroke="rgb(0, 0, 0)"\n   stroke-linecap="butt"\n   stroke-linejoin="miter"\n   stroke-width="0.350000"\n   transform="scale(1,-1)"\n  >\n<path id= "1" d=" M 6 122.5 L 6 0 " />\n<path id= "2" d=" M 8.80071 122.5 L 8.80071 116.646 " />\n<path id= "3" d=" M 6 116.646 L 8.80071 116.646 " />\n<path id= "4" d=" M 6 122.5 L 8.80071 122.5 " />\n<path id= "5" d=" M 3 122.5 L 6 122.5 " />\n<path id= "6" d=" M 6.88998 116.646 L 6.88998 116.645 " />\n<path id= "7" d=" M 6 116.645 L 6.88998 116.645 " />\n<path id= "8" d=" M 6.88998 116.645 L 6.88998 107.221 " />\n<path id= "9" d=" M 6 107.221 L 6.88998 107.221 " />\n<path id= "10" d=" M 3 0 L 6 0 " />\n<path id= "11" d=" M 3 0 L 3 122.5 " />\n<path id= "12" d=" M 3 5 L 0 5 " />\n<path d="M0,5 L0,5.03773  L0,5.15043  L0,5.3367  L0,5.59419  L0,5.91965  L0,6.30901  L0,6.75736  L0,7.25906  L0,7.80781  L0,8.3967  L0,9.01833  L0,9.66487  L0,10.3282  L0,11 " /><path id= "14" d=" M 3 117.5 L 0 117.5 " />\n<path id= "15" d=" M 0 117.5 L 0 11 " />\n</g>\n</g>
  Visible = false
  X = 660.75
  Y = 1263.02
FEATURE [Drawing::FeatureViewPart] Ortho028  label="Ortho_0_019"
  Direction = (0,0,1)
  HiddenWidth = 0.15
  LineWidth = 0.35
  Rotation = 90
  ShowHiddenLines = false
  ShowSmoothLines = false
  Source = -> Common009
  Tolerance = 0.05
  ViewResult = <g id="Ortho_0_019"\n   transform="rotate(90,660.75,451.453) translate(660.75,451.453) scale(1,1)"\n  >\n<g   fill="none"\n   stroke="rgb(0, 0, 0)"\n   stroke-linecap="butt"\n   stroke-linejoin="miter"\n   stroke-width="0.350000"\n   transform="scale(1,-1)"\n  >\n<path id= "1" d=" M -70.9342 -122.5 L -70.9359 -122.5 " />\n<path id= "2" d=" M -85.9402 -122.5 L -121.905 -122.5 " />\n<path id= "3" d=" M -121.905 0 L -121.905 -122.5 " />\n<path id= "4" d=" M 0 0 L -121.905 0 " />\n<path id= "5" d=" M 0 -122.5 L 0 0 " />\n<path id= "6" d=" M 0 -122.5 L -53.2924 -122.5 " />\n<path id= "7" d=" M -53.2924 -122.5 L -56.6721 -116.646 " />\n<path id= "8" d=" M -56.6721 -116.646 L -67.5544 -116.646 " />\n<path id= "9" d=" M -67.5544 -116.646 L -70.9342 -122.5 " />\n<path id= "10" d=" M -53.2924 -122.5 L -70.9342 -122.5 " />\n<path id= "11" d=" M -70.9359 -122.5 L -85.9402 -122.5 " />\n<path id= "12" d=" M -70.9359 -122.5 L -67.5558 -116.645 " />\n<path id= "13" d=" M -67.5558 -116.645 L -72.9969 -107.221 " />\n<path id= "14" d=" M -72.9969 -107.221 L -83.8792 -107.221 " />\n<path id= "15" d=" M -83.8792 -107.221 L -89.3203 -116.645 " />\n<path id= "16" d=" M -89.3203 -116.645 L -85.9402 -122.5 " />\n</g>\n</g>
  Visible = false
  X = 660.75
  Y = 451.453
FEATURE [Drawing::FeatureViewPart] Ortho029  label="Ortho_1_010"
  Direction = (0.57735,0.57735,0.57735)
  HiddenWidth = 0.15
  LineWidth = 0.35
  Rotation = 120
  ShowHiddenLines = false
  ShowSmoothLines = false
  Source = -> Common009
  Tolerance = 0.05
  ViewResult = <blob: 2231 chars omitted>
  Visible = false
  X = 1666.83
  Y = 443.982
FEATURE [Drawing::FeatureViewPart] Ortho030  label="Ortho_0_020"
  Direction = (1,0,0)
  HiddenWidth = 0.15
  LineWidth = 0.35
  Rotation = -90
  ShowHiddenLines = false
  ShowSmoothLines = false
  Source = -> Common010
  Tolerance = 0.05
  ViewResult = <g id="Ortho_0_020"\n   transform="rotate(-90,386.71,718.139) translate(386.71,718.139) scale(1,1)"\n  >\n<g   fill="none"\n   stroke="rgb(0, 0, 0)"\n   stroke-linecap="butt"\n   stroke-linejoin="miter"\n   stroke-width="0.350000"\n   transform="scale(1,-1)"\n  >\n<path id= "1" d=" M 6.79654 116.645 L 6.79654 107.221 " />\n<path id= "2" d=" M 6.79654 122.5 L 6.79654 116.645 " />\n<path id= "3" d=" M 6 107.221 L 6.79654 107.221 " />\n<path id= "4" d=" M 6 116.645 L 6.79654 116.645 " />\n<path id= "5" d=" M 6.79654 122.5 L 6 122.5 " />\n<path id= "6" d=" M 10.4071 122.5 L 6.79654 122.5 " />\n<path id= "7" d=" M 3 122.5 L 6 122.5 " />\n<path id= "8" d=" M 6 0 L 6 122.5 " />\n<path id= "9" d=" M 3 122.5 L 3 0 " />\n<path id= "10" d=" M 10.4071 122.5 L 10.4071 116.646 " />\n<path id= "11" d=" M 6.79654 116.646 L 10.4071 116.646 " />\n<path id= "12" d=" M 3 0 L 6 0 " />\n<path id= "13" d=" M 3 5 L 0 5 " />\n<path d="M0,5 L0,5.03773  L0,5.15043  L0,5.3367  L0,5.59419  L0,5.91965  L0,6.30901  L0,6.75736  L0,7.25906  L0,7.80781  L0,8.3967  L0,9.01833  L0,9.66487  L0,10.3282  L0,11 " /><path id= "15" d=" M 0 111.5 L 0 11 " />\n<path id= "16" d=" M 3 117.5 L 0 117.5 " />\n<path d="M0,111.5 L0,112.172  L0,112.835  L0,113.482  L0,114.103  L0,114.692  L0,115.241  L0,115.743  L0,116.191  L0,116.58  L0,116.906  L0,117.163  L0,117.35  L0,117.462  L0,117.5 " /></g>\n</g>
  Visible = false
  X = 386.71
  Y = 718.139
FEATURE [Drawing::FeatureViewPart] Ortho031  label="Ortho_0_021"
  Direction = (0,0,1)
  HiddenWidth = 0.15
  LineWidth = 0.35
  Rotation = 90
  ShowHiddenLines = false
  ShowSmoothLines = false
  Source = -> Common010
  Tolerance = 0.05
  ViewResult = <g id="Ortho_0_021"\n   transform="rotate(90,386.71,290.108) translate(386.71,290.108) scale(1,1)"\n  >\n<g   fill="none"\n   stroke="rgb(0, 0, 0)"\n   stroke-linecap="butt"\n   stroke-linejoin="miter"\n   stroke-width="0.350000"\n   transform="scale(1,-1)"\n  >\n<path id= "1" d=" M 63.0421 -116.645 L 57.601 -107.221 " />\n<path id= "2" d=" M 59.662 -122.5 L 63.0421 -116.645 " />\n<path id= "3" d=" M 44.6577 -122.5 L 59.662 -122.5 " />\n<path id= "4" d=" M 41.2775 -116.645 L 44.6577 -122.5 " />\n<path id= "5" d=" M 46.7187 -107.221 L 41.2775 -116.645 " />\n<path id= "6" d=" M 57.601 -107.221 L 46.7187 -107.221 " />\n<path id= "7" d=" M 0 -122.5 L 27.0142 -122.5 " />\n<path id= "8" d=" M 27.0142 -122.5 L 44.656 -122.5 " />\n<path id= "9" d=" M 44.656 -122.5 L 44.6577 -122.5 " />\n<path id= "10" d=" M 59.662 -122.5 L 121.905 -122.5 " />\n<path id= "11" d=" M 0 -122.5 L 0 0 " />\n<path id= "12" d=" M 0 0 L 121.905 0 " />\n<path id= "13" d=" M 121.905 0 L 121.905 -122.5 " />\n<path id= "14" d=" M 30.394 -116.646 L 27.0142 -122.5 " />\n<path id= "15" d=" M 44.656 -122.5 L 41.2763 -116.646 " />\n<path id= "16" d=" M 41.2763 -116.646 L 30.394 -116.646 " />\n</g>\n</g>
  Visible = false
  X = 386.71
  Y = 290.108
FEATURE [Drawing::FeatureViewPart] Ortho032  label="Ortho_1_011"
  Direction = (0.57735,0.57735,0.57735)
  HiddenWidth = 0.15
  LineWidth = 0.35
  Rotation = 120
  ShowHiddenLines = false
  ShowSmoothLines = false
  Source = -> Common010
  Tolerance = 0.05
  ViewResult = <blob: 2175 chars omitted>
  Visible = false
  X = 961.14
  Y = 355.431
FEATURE [Drawing::FeatureViewPart] Ortho033  label="Ortho_0_022"
  Direction = (1,0,0)
  HiddenWidth = 0.15
  LineWidth = 0.35
  Rotation = -90
  ShowHiddenLines = false
  ShowSmoothLines = false
  Source = -> Common011
  Tolerance = 0.05
  ViewResult = <g id="Ortho_0_022"\n   transform="rotate(-90,660.75,1288.93) translate(660.75,1288.93) scale(1,1)"\n  >\n<g   fill="none"\n   stroke="rgb(0, 0, 0)"\n   stroke-linecap="butt"\n   stroke-linejoin="miter"\n   stroke-width="0.350000"\n   transform="scale(1,-1)"\n  >\n<path id= "1" d=" M 6 -5.68434e-14 L 6 122.5 " />\n<path id= "2" d=" M 3 122.5 L 6 122.5 " />\n<path id= "3" d=" M 3 0 L 6 0 " />\n<path id= "4" d=" M 3 122.5 L 3 0 " />\n<path id= "5" d=" M 6 60.094 L 8.84765 60.094 " />\n<path id= "6" d=" M 8.84765 60.094 L 8.84765 50.6697 " />\n<path id= "7" d=" M 6 50.6697 L 8.84765 50.6697 " />\n<path id= "8" d=" M 8.84765 50.6697 L 8.84765 41.2454 " />\n<path id= "9" d=" M 6 41.2454 L 8.84765 41.2454 " />\n<path id= "10" d=" M 6 88.3693 L 11.1099 88.3693 " />\n<path id= "11" d=" M 11.1099 88.3693 L 11.1099 78.945 " />\n<path id= "12" d=" M 6 78.945 L 11.1099 78.945 " />\n<path id= "13" d=" M 11.1099 78.945 L 11.1099 69.5207 " />\n<path id= "14" d=" M 6 69.5207 L 11.1099 69.5207 " />\n<path id= "15" d=" M 3 5 L 0 5 " />\n<path d="M0,5 L0,5.03773  L0,5.15043  L0,5.3367  L0,5.59419  L0,5.91965  L0,6.30901  L0,6.75736  L0,7.25906  L0,7.80781  L0,8.3967  L0,9.01833  L0,9.66487  L0,10.3282  L0,11 " /><path id= "17" d=" M 0 111.5 L 0 11 " />\n<path id= "18" d=" M 3 117.5 L 0 117.5 " />\n<path d="M0,111.5 L0,112.172  L0,112.835  L0,113.482  L0,114.103  L0,114.692  L0,115.241  L0,115.743  L0,116.191  L0,116.58  L0,116.906  L0,117.163  L0,117.35  L0,117.462  L0,117.5 " /></g>\n</g>
  Visible = false
  X = 660.75
  Y = 1288.93
FEATURE [Drawing::FeatureViewPart] Ortho034  label="Ortho_0_023"
  Direction = (0,0,1)
  HiddenWidth = 0.15
  LineWidth = 0.35
  Rotation = 90
  ShowHiddenLines = false
  ShowSmoothLines = false
  Source = -> Common011
  Tolerance = 0.05
  ViewResult = <g id="Ortho_0_023"\n   transform="rotate(90,660.75,204.547) translate(660.75,204.547) scale(1,1)"\n  >\n<g   fill="none"\n   stroke="rgb(0, 0, 0)"\n   stroke-linecap="butt"\n   stroke-linejoin="miter"\n   stroke-width="0.350000"\n   transform="scale(1,-1)"\n  >\n<path id= "1" d=" M 250 5.68434e-14 L 250 -122.5 " />\n<path id= "2" d=" M 121.905 -122.5 L 250 -122.5 " />\n<path id= "3" d=" M 121.905 0 L 121.905 -122.5 " />\n<path id= "4" d=" M 250 0 L 121.905 0 " />\n<path id= "5" d=" M 128.342 -60.094 L 139.225 -60.094 " />\n<path id= "6" d=" M 139.225 -60.094 L 144.666 -50.6697 " />\n<path id= "7" d=" M 122.901 -50.6697 L 128.342 -60.094 " />\n<path id= "8" d=" M 144.666 -50.6697 L 139.225 -41.2454 " />\n<path id= "9" d=" M 128.342 -41.2454 L 122.901 -50.6697 " />\n<path id= "10" d=" M 139.225 -41.2454 L 128.342 -41.2454 " />\n<path id= "11" d=" M 144.667 -88.3693 L 155.549 -88.3693 " />\n<path id= "12" d=" M 155.549 -88.3693 L 160.991 -78.945 " />\n<path id= "13" d=" M 139.226 -78.945 L 144.667 -88.3693 " />\n<path id= "14" d=" M 160.991 -78.945 L 155.549 -69.5207 " />\n<path id= "15" d=" M 144.667 -69.5207 L 139.226 -78.945 " />\n<path id= "16" d=" M 155.549 -69.5207 L 144.667 -69.5207 " />\n</g>\n</g>
  Visible = false
  X = 660.75
  Y = 204.547
FEATURE [Drawing::FeatureViewPart] Ortho035  label="Ortho_1_012"
  Direction = (0.57735,0.57735,0.57735)
  HiddenWidth = 0.15
  LineWidth = 0.35
  Rotation = 120
  ShowHiddenLines = false
  ShowSmoothLines = false
  Source = -> Common011
  Tolerance = 0.05
  ViewResult = <blob: 2485 chars omitted>
  Visible = false
  X = 1866.18
  Y = 344.126
FEATURE [Drawing::FeatureViewPart] Ortho036  label="Ortho_0_024"
  Direction = (1,0,0)
  HiddenWidth = 0.15
  LineWidth = 0.35
  Rotation = -90
  ShowHiddenLines = false
  ShowSmoothLines = false
  Source = -> Common012
  Tolerance = 0.05
  ViewResult = <g id="Ortho_0_024"\n   transform="rotate(-90,506.79,687.126) translate(506.79,687.126) scale(1,1)"\n  >\n<g   fill="none"\n   stroke="rgb(0, 0, 0)"\n   stroke-linecap="butt"\n   stroke-linejoin="miter"\n   stroke-width="0.350000"\n   transform="scale(1,-1)"\n  >\n<path id= "1" d=" M 6 250 L 6 122.5 " />\n<path id= "2" d=" M 3 122.5 L 6 122.5 " />\n<path id= "3" d=" M 3 122.5 L 3 250 " />\n<path id= "4" d=" M 3 250 L 6 250 " />\n<path id= "5" d=" M 3 127.5 L 0 127.5 " />\n<path id= "6" d=" M 3 240 L 0 240 " />\n<path id= "7" d=" M 0 240 L 0 127.5 " />\n</g>\n</g>
  Visible = false
  X = 506.79
  Y = 687.126
FEATURE [Drawing::FeatureViewPart] Ortho037  label="Ortho_0_025"
  Direction = (0,0,1)
  HiddenWidth = 0.15
  LineWidth = 0.35
  Rotation = 90
  ShowHiddenLines = false
  ShowSmoothLines = false
  Source = -> Common012
  Tolerance = 0.05
  ViewResult = <g id="Ortho_0_025"\n   transform="rotate(90,506.79,527.016) translate(506.79,527.016) scale(1,1)"\n  >\n<g   fill="none"\n   stroke="rgb(0, 0, 0)"\n   stroke-linecap="butt"\n   stroke-linejoin="miter"\n   stroke-width="0.350000"\n   transform="scale(1,-1)"\n  >\n<path id= "1" d=" M -250 -250 L -250 -122.5 " />\n<path id= "2" d=" M -121.905 -122.5 L -250 -122.5 " />\n<path id= "3" d=" M -121.905 -250 L -121.905 -122.5 " />\n<path id= "4" d=" M -121.905 -250 L -250 -250 " />\n</g>\n</g>
  Visible = false
  X = 506.79
  Y = 527.016
FEATURE [Drawing::FeatureViewPart] Ortho038  label="Ortho_1_013"
  Direction = (0.57735,0.57735,0.57735)
  HiddenWidth = 0.15
  LineWidth = 0.35
  Rotation = 120
  ShowHiddenLines = false
  ShowSmoothLines = false
  Source = -> Common012
  Tolerance = 0.05
  ViewResult = <g id="Ortho_1_013"\n   transform="rotate(120,877.48,495.464) translate(877.48,495.464) scale(1,1)"\n  >\n<g   fill="none"\n   stroke="rgb(0, 0, 0)"\n   stroke-linecap="butt"\n   stroke-linejoin="miter"\n   stroke-width="0.350000"\n   transform="scale(1,-1)"\n  >\n<path id= "1" d=" M -181.019 -104.512 L -181.019 -0.408248 " />\n<path id= "2" d=" M -90.4426 -52.7027 L -181.019 -0.408248 " />\n<path id= "3" d=" M -90.4426 -156.806 L -90.4426 -52.7027 " />\n<path id= "4" d=" M -90.4426 -156.806 L -181.019 -104.512 " />\n<path id= "5" d=" M -178.898 0.816497 L -181.019 -0.408248 " />\n<path id= "6" d=" M -178.898 0.816497 L -88.3213 -51.478 " />\n<path id= "7" d=" M -88.3213 -51.478 L -90.4426 -52.7027 " />\n<path id= "8" d=" M -88.3213 -51.478 L -88.3213 -155.581 " />\n<path id= "9" d=" M -88.3213 -155.581 L -90.4426 -156.806 " />\n</g>\n</g>
  Visible = false
  X = 877.48
  Y = 495.464
FEATURE [Drawing::FeatureViewPart] Ortho039  label="Ortho_0_026"
  Direction = (1,0,0)
  HiddenWidth = 0.15
  LineWidth = 0.35
  Rotation = -90
  ShowHiddenLines = false
  ShowSmoothLines = false
  Source = -> Common013
  Tolerance = 0.05
  ViewResult = <g id="Ortho_0_026"\n   transform="rotate(-90,785.75,1267.45) translate(785.75,1267.45) scale(1,1)"\n  >\n<g   fill="none"\n   stroke="rgb(0, 0, 0)"\n   stroke-linecap="butt"\n   stroke-linejoin="miter"\n   stroke-width="0.350000"\n   transform="scale(1,-1)"\n  >\n<path id= "1" d=" M 3 250 L 6 250 " />\n<path id= "2" d=" M 3 250 L 3 122.5 " />\n<path id= "3" d=" M 6 122.5 L 6 250 " />\n<path id= "4" d=" M 3 122.5 L 6 122.5 " />\n<path id= "5" d=" M 8.80071 122.5 L 6 122.5 " />\n<path id= "6" d=" M 3 127.5 L 0 127.5 " />\n<path d="M0,127.5 L0,127.544  L0,127.676  L0,127.893  L0,128.193  L0,128.573  L0,129.027  L0,129.55  L0,130.136  L0,130.776  L0,131.463  L0,132.188  L0,132.942  L0,133.716  L0,134.5 " /><path id= "8" d=" M 3 240 L 0 240 " />\n<path id= "9" d=" M 0 240 L 0 134.5 " />\n<path id= "10" d=" M 8.80071 126.071 L 8.80071 126.07 " />\n<path id= "11" d=" M 6 126.07 L 8.80071 126.07 " />\n<path id= "12" d=" M 8.80071 126.07 L 8.80071 122.5 " />\n<path id= "13" d=" M 6 144.92 L 17.6493 144.92 " />\n<path id= "14" d=" M 17.6493 144.92 L 17.6493 135.496 " />\n<path id= "15" d=" M 6 135.496 L 17.6493 135.496 " />\n<path id= "16" d=" M 17.6493 135.496 L 17.6493 126.071 " />\n<path id= "17" d=" M 6 126.071 L 17.6493 126.071 " />\n<path id= "18" d=" M 6 173.195 L 6.31531 173.195 " />\n<path id= "19" d=" M 6.31531 173.195 L 6.31531 163.771 " />\n<path id= "20" d=" M 6 163.771 L 6.31531 163.771 " />\n<path id= "21" d=" M 6.31531 163.771 L 6.31531 154.346 " />\n<path id= "22" d=" M 6 154.346 L 6.31531 154.346 " />\n<path id= "23" d=" M 6.31531 163.77 L 15.0248 163.77 " />\n<path id= "24" d=" M 15.0248 163.77 L 15.0248 154.346 " />\n<path id= "25" d=" M 6 154.346 L 15.0248 154.346 " />\n<path id= "26" d=" M 15.0248 154.346 L 15.0248 144.921 " />\n<path id= "27" d=" M 6 144.921 L 15.0248 144.921 " />\n</g>\n</g>
  Visible = false
  X = 785.75
  Y = 1267.45
FEATURE [Drawing::FeatureViewPart] Ortho040  label="Ortho_0_027"
  Direction = (0,0,1)
  HiddenWidth = 0.15
  LineWidth = 0.35
  Rotation = 90
  ShowHiddenLines = false
  ShowSmoothLines = false
  Source = -> Common013
  Tolerance = 0.05
  ViewResult = <blob: 2343 chars omitted>
  Visible = false
  X = 785.75
  Y = 451.453
FEATURE [Drawing::FeatureViewPart] Ortho041  label="Ortho_1_014"
  Direction = (0.57735,0.57735,0.57735)
  HiddenWidth = 0.15
  LineWidth = 0.35
  Rotation = 120
  ShowHiddenLines = false
  ShowSmoothLines = false
  Source = -> Common013
  Tolerance = 0.05
  ViewResult = <blob: 4527 chars omitted>
  Visible = false
  X = 1755.22
  Y = 498.625
FEATURE [Drawing::FeatureViewPart] Ortho042  label="Ortho_0_028"
  Direction = (1,0,0)
  HiddenWidth = 0.15
  LineWidth = 0.35
  Rotation = -90
  ShowHiddenLines = false
  ShowSmoothLines = false
  Source = -> Common014
  Tolerance = 0.05
  ViewResult = <g id="Ortho_0_028"\n   transform="rotate(-90,785.75,1263.82) translate(785.75,1263.82) scale(1,1)"\n  >\n<g   fill="none"\n   stroke="rgb(0, 0, 0)"\n   stroke-linecap="butt"\n   stroke-linejoin="miter"\n   stroke-width="0.350000"\n   transform="scale(1,-1)"\n  >\n<path id= "1" d=" M 3 250 L 6 250 " />\n<path id= "2" d=" M 3 250 L 3 122.5 " />\n<path id= "3" d=" M 6 122.5 L 6 250 " />\n<path id= "4" d=" M 3 122.5 L 6 122.5 " />\n<path id= "5" d=" M 6.79654 122.5 L 10.4071 122.5 " />\n<path id= "6" d=" M 6 122.5 L 6.79654 122.5 " />\n<path id= "7" d=" M 3 127.5 L 0 127.5 " />\n<path d="M0,127.5 L0,127.544  L0,127.676  L0,127.893  L0,128.193  L0,128.573  L0,129.027  L0,129.55  L0,130.136  L0,130.776  L0,131.463  L0,132.188  L0,132.942  L0,133.716  L0,134.5 " /><path id= "9" d=" M 0 233 L 0 134.5 " />\n<path id= "10" d=" M 3 240 L 0 240 " />\n<path d="M0,233 L0,233.784  L0,234.558  L0,235.312  L0,236.037  L0,236.724  L0,237.364  L0,237.95  L0,238.473  L0,238.927  L0,239.307  L0,239.607  L0,239.824  L0,239.956  L0,240 " /><path id= "12" d=" M 7.11976 135.495 L 10.4071 135.495 " />\n<path id= "13" d=" M 10.4071 135.495 L 10.4071 126.07 " />\n<path id= "14" d=" M 6 126.07 L 10.4071 126.07 " />\n<path id= "15" d=" M 10.4071 126.07 L 10.4071 122.5 " />\n<path id= "16" d=" M 6 126.07 L 6.79654 126.07 " />\n<path id= "17" d=" M 6.79654 126.07 L 6.79654 122.5 " />\n<path id= "18" d=" M 6 144.92 L 7.11976 144.92 " />\n<path id= "19" d=" M 7.11976 144.92 L 7.11976 135.496 " />\n<path id= "20" d=" M 6 135.496 L 7.11976 135.496 " />\n<path id= "21" d=" M 7.11976 135.496 L 7.11976 126.071 " />\n<path id= "22" d=" M 6 126.071 L 7.11976 126.071 " />\n</g>\n</g>
  Visible = false
  X = 785.75
  Y = 1263.82
FEATURE [Drawing::FeatureViewPart] Ortho043  label="Ortho_0_029"
  Direction = (0,0,1)
  HiddenWidth = 0.15
  LineWidth = 0.35
  Rotation = 90
  ShowHiddenLines = false
  ShowSmoothLines = false
  Source = -> Common014
  Tolerance = 0.05
  ViewResult = <g id="Ortho_0_029"\n   transform="rotate(90,785.75,329.547) translate(785.75,329.547) scale(1,1)"\n  >\n<g   fill="none"\n   stroke="rgb(0, 0, 0)"\n   stroke-linecap="butt"\n   stroke-linejoin="miter"\n   stroke-width="0.350000"\n   transform="scale(1,-1)"\n  >\n<path id= "1" d=" M 121.905 -250 L 5.68434e-14 -250 " />\n<path id= "2" d=" M 0 -122.5 L 0 -250 " />\n<path id= "3" d=" M 27.0142 -122.5 L 0 -122.5 " />\n<path id= "4" d=" M 44.6577 -122.5 L 44.656 -122.5 " />\n<path id= "5" d=" M 121.905 -122.5 L 59.662 -122.5 " />\n<path id= "6" d=" M 121.905 -122.5 L 121.905 -250 " />\n<path id= "7" d=" M 44.656 -122.5 L 27.0142 -122.5 " />\n<path id= "8" d=" M 59.662 -122.5 L 44.6577 -122.5 " />\n<path id= "9" d=" M 27.0142 -122.5 L 24.9528 -126.07 " />\n<path id= "10" d=" M 24.9528 -126.07 L 30.394 -135.495 " />\n<path id= "11" d=" M 30.394 -135.495 L 41.2763 -135.495 " />\n<path id= "12" d=" M 41.2763 -135.495 L 46.7174 -126.07 " />\n<path id= "13" d=" M 46.7174 -126.07 L 44.656 -122.5 " />\n<path id= "14" d=" M 44.6577 -122.5 L 46.7187 -126.07 " />\n<path id= "15" d=" M 46.7187 -126.07 L 57.601 -126.07 " />\n<path id= "16" d=" M 57.601 -126.07 L 59.662 -122.5 " />\n<path id= "17" d=" M 46.7187 -144.92 L 57.601 -144.92 " />\n<path id= "18" d=" M 57.601 -144.92 L 63.0421 -135.496 " />\n<path id= "19" d=" M 41.2775 -135.496 L 46.7187 -144.92 " />\n<path id= "20" d=" M 63.0421 -135.496 L 57.601 -126.071 " />\n<path id= "21" d=" M 46.7187 -126.071 L 41.2775 -135.496 " />\n<path id= "22" d=" M 57.601 -126.071 L 46.7187 -126.071 " />\n</g>\n</g>
  Visible = false
  X = 785.75
  Y = 329.547
FEATURE [Drawing::FeatureViewPart] Ortho044  label="Ortho_1_015"
  Direction = (0.57735,0.57735,0.57735)
  HiddenWidth = 0.15
  LineWidth = 0.35
  Rotation = 120
  ShowHiddenLines = false
  ShowSmoothLines = false
  Source = -> Common014
  Tolerance = 0.05
  ViewResult = <blob: 2913 chars omitted>
  Visible = false
  X = 1841.42
  Y = 445.901
FEATURE [Drawing::FeatureViewPart] Ortho045  label="Ortho_0_030"
  Direction = (1,0,0)
  HiddenWidth = 0.15
  LineWidth = 0.35
  Rotation = -90
  ShowHiddenLines = false
  ShowSmoothLines = false
  Source = -> Common015
  Tolerance = 0.05
  ViewResult = <g id="Ortho_0_030"\n   transform="rotate(-90,785.75,1287.95) translate(785.75,1287.95) scale(1,1)"\n  >\n<g   fill="none"\n   stroke="rgb(0, 0, 0)"\n   stroke-linecap="butt"\n   stroke-linejoin="miter"\n   stroke-width="0.350000"\n   transform="scale(1,-1)"\n  >\n<path id= "1" d=" M 6 122.5 L 6 201.472 " />\n<path id= "2" d=" M 6 220.321 L 6 250 " />\n<path id= "3" d=" M 3 122.5 L 6 122.5 " />\n<path id= "4" d=" M 3 250 L 5.16883 250 " />\n<path id= "5" d=" M 5.16883 239.172 L 5.16883 250 " />\n<path id= "6" d=" M 5.6037 239.172 L 5.16883 239.172 " />\n<path id= "7" d=" M 5.6037 250 L 5.6037 239.172 " />\n<path id= "8" d=" M 5.6037 250 L 6 250 " />\n<path id= "9" d=" M 5.16883 220.321 L 6 220.321 " />\n<path id= "10" d=" M 5.16883 201.472 L 5.16883 220.321 " />\n<path id= "11" d=" M 6 201.472 L 5.16883 201.472 " />\n<path id= "12" d=" M 3 250 L 3 122.5 " />\n<path id= "13" d=" M 6 201.472 L 9.14557 201.472 " />\n<path id= "14" d=" M 9.14557 220.321 L 6 220.321 " />\n<path id= "15" d=" M 5.6037 250 L 5.16883 250 " />\n<path id= "16" d=" M 9.14557 201.472 L 9.14557 220.321 " />\n<path id= "17" d=" M 3 127.5 L 0 127.5 " />\n<path d="M0,127.5 L0,127.544  L0,127.676  L0,127.893  L0,128.193  L0,128.573  L0,129.027  L0,129.55  L0,130.136  L0,130.776  L0,131.463  L0,132.188  L0,132.942  L0,133.716  L0,134.5 " /><path id= "19" d=" M 0 233 L 0 134.5 " />\n<path id= "20" d=" M 3 240 L 0 240 " />\n<path d="M0,233 L0,233.784  L0,234.558  L0,235.312  L0,236.037  L0,236.724  L0,237.364  L0,237.95  L0,238.473  L0,238.927  L0,239.307  L0,239.607  L0,239.824  L0,239.956  L0,240 " /></g>\n</g>
  Visible = false
  X = 785.75
  Y = 1287.95
FEATURE [Drawing::FeatureViewPart] Ortho046  label="Ortho_0_031"
  Direction = (0,0,1)
  HiddenWidth = 0.15
  LineWidth = 0.35
  Rotation = 90
  ShowHiddenLines = false
  ShowSmoothLines = false
  Source = -> Common015
  Tolerance = 0.05
  ViewResult = <g id="Ortho_0_031"\n   transform="rotate(90,785.75,204.547) translate(785.75,204.547) scale(1,1)"\n  >\n<g   fill="none"\n   stroke="rgb(0, 0, 0)"\n   stroke-linecap="butt"\n   stroke-linejoin="miter"\n   stroke-width="0.350000"\n   transform="scale(1,-1)"\n  >\n<path id= "1" d=" M 121.905 -250 L 121.905 -122.5 " />\n<path id= "2" d=" M 121.905 -122.5 L 250 -122.5 " />\n<path id= "3" d=" M 250 -122.5 L 250 -201.472 " />\n<path id= "4" d=" M 250 -220.321 L 250 -250 " />\n<path id= "5" d=" M 250 -250 L 121.905 -250 " />\n<path id= "6" d=" M 250 -201.472 L 242.615 -201.472 " />\n<path id= "7" d=" M 242.615 -201.472 L 237.174 -210.896 " />\n<path id= "8" d=" M 237.174 -210.896 L 242.615 -220.321 " />\n<path id= "9" d=" M 242.615 -220.321 L 250 -220.321 " />\n<path id= "10" d=" M 250 -201.472 L 250 -220.321 " />\n</g>\n</g>
  Visible = false
  X = 785.75
  Y = 204.547
FEATURE [Drawing::FeatureViewPart] Ortho047  label="Ortho_1_016"
  Direction = (0.57735,0.57735,0.57735)
  HiddenWidth = 0.15
  LineWidth = 0.35
  Rotation = 120
  ShowHiddenLines = false
  ShowSmoothLines = false
  Source = -> Common015
  Tolerance = 0.05
  ViewResult = <g id="Ortho_1_016"\n   transform="rotate(120,1954.57,394.355) translate(1954.57,394.355) scale(1,1)"\n  >\n<g   fill="none"\n   stroke="rgb(0, 0, 0)"\n   stroke-linecap="butt"\n   stroke-linejoin="miter"\n   stroke-width="0.350000"\n   transform="scale(1,-1)"\n  >\n<path id= "1" d=" M 81.9574 -256.341 L 81.9574 -152.238 " />\n<path id= "2" d=" M 81.9574 -152.238 L 172.534 -204.532 " />\n<path id= "3" d=" M 172.534 -204.532 L 172.534 -269.013 " />\n<path id= "4" d=" M 167.312 -265.998 L 172.534 -269.013 " />\n<path id= "5" d=" M 172.534 -284.403 L 172.534 -308.636 " />\n<path id= "6" d=" M 172.534 -308.636 L 81.9574 -256.341 " />\n<path id= "7" d=" M 84.0787 -151.013 L 81.9574 -152.238 " />\n<path id= "8" d=" M 174.655 -203.308 L 84.0787 -151.013 " />\n<path id= "9" d=" M 174.655 -203.308 L 172.534 -204.532 " />\n<path id= "10" d=" M 174.655 -307.411 L 173.122 -308.296 " />\n<path id= "11" d=" M 173.122 -299.456 L 173.122 -308.296 " />\n<path id= "12" d=" M 172.814 -299.633 L 173.122 -299.456 " />\n<path id= "13" d=" M 172.814 -308.474 L 172.814 -299.633 " />\n<path id= "14" d=" M 172.814 -308.474 L 172.534 -308.636 " />\n<path id= "15" d=" M 173.122 -284.063 L 172.534 -284.403 " />\n<path id= "16" d=" M 173.122 -268.673 L 173.122 -284.063 " />\n<path id= "17" d=" M 172.534 -269.013 L 173.122 -268.673 " />\n<path id= "18" d=" M 174.655 -307.411 L 174.655 -203.308 " />\n<path id= "19" d=" M 170.31 -270.297 L 165.088 -267.282 " />\n<path id= "20" d=" M 167.312 -265.998 L 165.088 -267.282 " />\n<path id= "21" d=" M 172.534 -269.013 L 170.31 -270.297 " />\n<path id= "22" d=" M 165.088 -267.282 L 161.241 -272.756 " />\n<path id= "23" d=" M 161.241 -272.756 L 165.088 -282.672 " />\n<path id= "24" d=" M 165.088 -282.672 L 170.31 -285.687 " />\n<path id= "25" d=" M 170.31 -285.687 L 172.534 -284.403 " />\n<path id= "26" d=" M 172.814 -308.474 L 173.122 -308.296 " />\n<path id= "27" d=" M 170.31 -270.297 L 170.31 -285.687 " />\n</g>\n</g>
  Visible = false
  X = 1954.57
  Y = 394.355
FEATURE [Drawing::FeaturePage] Page
  EditableTexts = AUTHOR NAME | DRAWING TITLE | FreeCAD DRAWING | A0 | X / Y | SCALE | PN | DN | DD/MM/YYYY | REV A
  Group = -> [Ortho,Ortho001,Ortho002,Ortho003,Ortho004,Ortho005,Ortho006,Ortho007,Ortho008,Ortho009,Ortho010,Ortho011,Ortho012,Ortho013,Ortho014,Ortho015,Ortho016,Ortho017,Ortho018,Ortho019,Ortho020,Ortho021,Ortho022,Ortho023,Ortho024,Ortho025,Ortho026,Ortho027,Ortho028,Ortho029,Ortho030,Ortho031,Ortho032,Ortho033,Ortho034,Ortho035,Ortho036,Ortho037,Ortho038,Ortho039,Ortho040,Ortho041,Ortho042,Ortho043,+4 more]
  Template = <path>
note: 1 file-system path scrubbed to <path> (originals preserved in the JSON sidecar)
